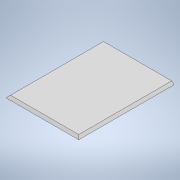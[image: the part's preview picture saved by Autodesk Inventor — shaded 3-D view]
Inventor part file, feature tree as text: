
AUTODESK INVENTOR PART (.ipt)
format: ipt  version: 2022 (Build 260153000, 153)  size: 95,744 bytes
history: native  units: mm
features: extrude x1, chamfer x1, sketch x1
ambient origin geometry x8: Origin, YZ Plane, XZ Plane, XY Plane, X Axis, Y Axis, Z Axis, Center Point
bodies: Solid1 (feature_tree)
feature tree (3):
  extrude  "Extrusion1"  Depth=1.0mm
  chamfer  "Chamfer1"  Distance=1.0mm
  sketch  "Sketch1"  dims[d0=41.9mm d1=32.0mm d2=1.0mm d3=0.0mm d4=1.0mm d5=2.0mm d6=45.0deg]
